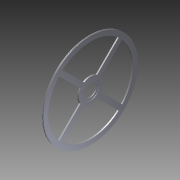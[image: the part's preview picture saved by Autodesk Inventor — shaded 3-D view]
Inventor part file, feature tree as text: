
AUTODESK INVENTOR PART (.ipt)
format: ipt  version: 2012 SP2 (Build 160219200, 219)  size: 169,472 bytes
history: native  units: in
note: dims shown in document units (in); Inventor stores cm internally (conversion verified against a paired STEP export)
features: sketch x2, revolve x1, mirror x1, fillet x1, extrude x1, reference x1
ambient origin geometry x8: Origin, YZ Plane, XZ Plane, XY Plane, X Axis, Y Axis, Z Axis, Center Point
bodies: Solid1 (feature_tree)
feature tree (7):
  revolve  "Revolution1"  [1 undecoded]
  mirror  "Mirror1"
  fillet  "Fillet1"  Radius=0.0591in
  extrude  "Extrusion1"  Depth=2.5591in
  sketch  "Sketch1"  dims[d0=0.0197in d1=0.0276in d2=0.0591in]
  reference  "Reference1"
  sketch  "Sketch2"  dims[d3=0.0276in d4=2.5591in d5=0.1575in d6=0.0197in d7=0.1181in d8=0.3937in d9=0.0118in d10=0.0031in d11=90.0deg d12=0.0197in d14=0.315in d15=0.1969in d16=45.0deg d17=0.1575in d18=1.5748in d20=360.0deg d22=0.3937in d23=0.0in]
note: 1 required parameter value undecoded (feature->parameter linkage not recoverable at this tier; creation-order binding heuristic only, values carry confidence <= 0.55)
